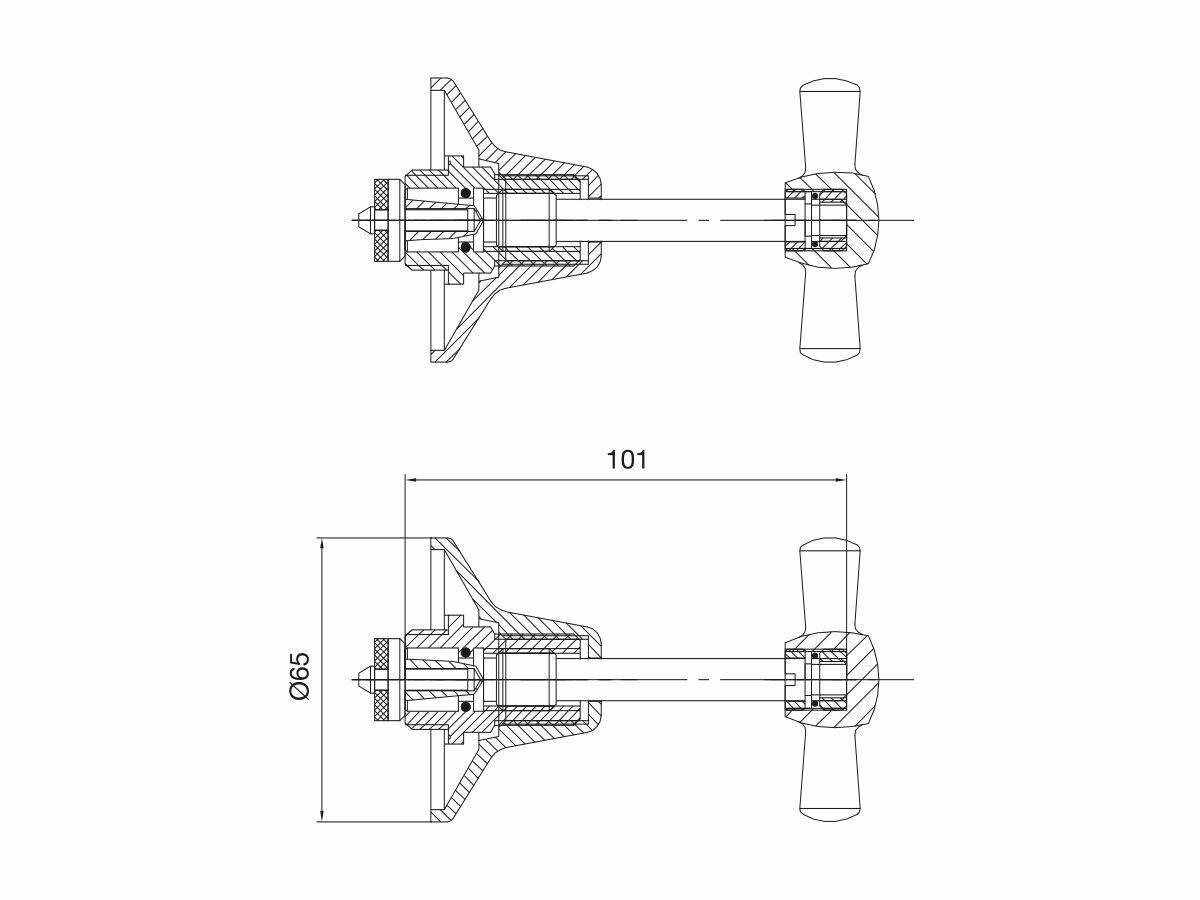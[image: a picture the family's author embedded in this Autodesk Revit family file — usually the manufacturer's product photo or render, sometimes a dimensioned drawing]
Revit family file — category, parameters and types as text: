
# Revit family: Reece_Shower_Base_Shower Set_Anti-Vandal
name_source: partatom
category: Plumbing Fixtures
revit_build: Autodesk Revit 2018 (Build: 20190510_1515(x64)
units: mm (PartAtom-declared; Revit-internal decimal feet)

## family parameters
Always vertical = Yes
Cut with Voids When Loaded = Yes
Part Type = Normal
Room Calculation Point = Yes
Round Connector Dimension = Use Diameter
Shared = Yes
Work Plane-Based = Yes

## types (1)
- Chrome
    Default Elevation = 0 mm  [stored 0 ft]
    Description = Base Shower Set Anti-Vandal Chrome (3 Star)
    Disclaimer = THIS FILE IS THE PROPERTY OF THE REECE GROUP. IT MAY NOT BE REPRODUCED, REVERSE-ENGINEERED OR MODIFIED. ANY REPUBLICATION, TRANSMISSION OR DISTRIBUTION FOR THE PURPOSE OF COMMERCIALLY EXPLOITING THE FILES IS PROHIBITED.
    Keynote = Product #9505432, Reece_Shower_Base_Shower Set_Anti-Vandal - Chrome
    Manufacturer = Base
    Model = Base
    Reece_Detail_Additional = Anti-Vandal
    Reece_Detail_Disclaimer = THIS FILE IS THE PROPERTY OF THE REECE GROUP. IT MAY NOT BE REPRODUCED, REVERSE-ENGINEERED OR MODIFIED. ANY REPUBLICATION, TRANSMISSION OR DISTRIBUTION FOR THE PURPOSE OF COMMERCIALLY EXPLOITING THE FILES IS PROHIBITED.
    Reece_Detail_Installation = Shower Set
    Reece_Material_Colour = Reece_Plastic_White
    Reece_Material_Main = Reece_Brass_Chrome
    Reece_Material_Secondary = Reece_Brass_Chrome
    Reece_Product_Brand = Base
    Reece_Product_Description = Base Shower Set Anti-Vandal Chrome (3 Star)
    Reece_Product_Mount = Wall Mounted
    Reece_Product_Number = 9505432
    Reece_Product_Sub Brand = Base
    Reece_Product_Type = Shower
    Reece_Product_Web Page = https://www.reece.com.au
    Reece_Shower_Head_Width = 80 mm  [stored 0.262467 ft]
    Reece_Shower_Inlet = 12 mm  [stored 0.0393701 ft]
    Reece_Shower_Reach = 228 mm  [stored 0.748031 ft]
    Type Comments = Shower
    URL = https://www.reece.com.au

note: [stored X ft] marks values corroborated as IEEE doubles in the binary element streams (Revit-internal decimal feet)

## geometry (parser evidence)
native form markers: Sweep x9
no freeform markers — native parametric forms only
